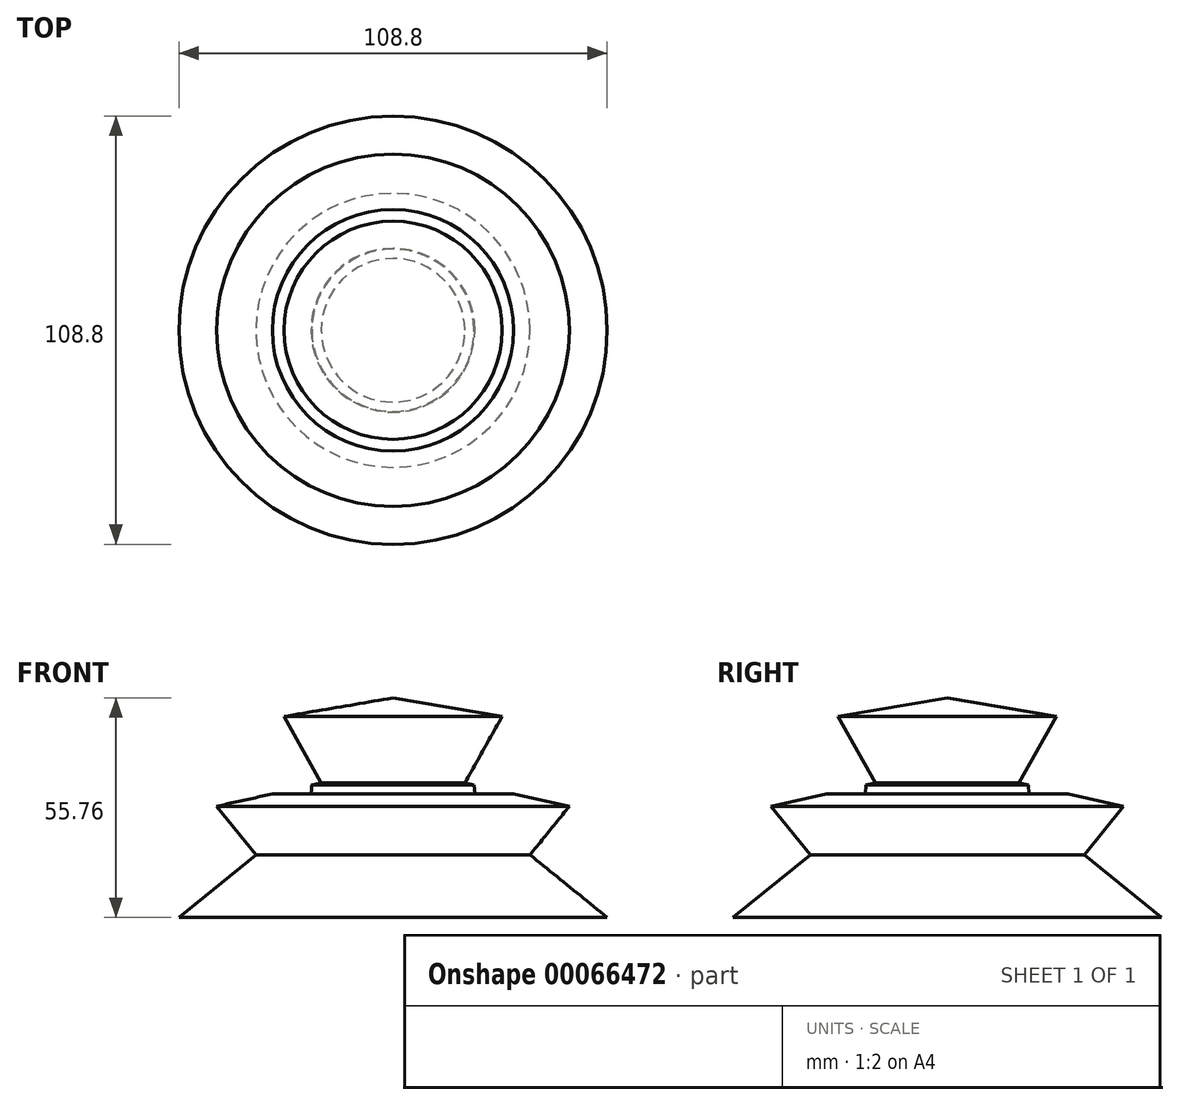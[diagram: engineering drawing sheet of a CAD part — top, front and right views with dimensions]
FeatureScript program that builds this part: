
annotation { "Feature Type Name" : "Feature", "Feature Type Description" : "" }
export const myFeature = defineFeature(function(context is Context, id is Id, definition is map)
    precondition{}
    {
        {
            var Q0;
            Q0=qCreatedBy(makeId("Front.planeOp"),FACE);
            var sketch = newSketch(context, id + "F0", { "sketchPlane" : qUnion([Q0])});
            skLineSegment(sketch, "E0", {"start": v(0, 55.76) * mm, "end": v(0, 0) * mm});
            skLineSegment(sketch, "E1", {"start": v(0, 0) * mm, "end": v(54.4, 0) * mm});
            skLineSegment(sketch, "E2", {"start": v(54.4, 0) * mm, "end": v(34.8, 15.88) * mm});
            skLineSegment(sketch, "E3", {"start": v(34.8, 15.88) * mm, "end": v(44.8, 28.21) * mm});
            skLineSegment(sketch, "E4", {"start": v(44.8, 28.21) * mm, "end": v(18.25, 34.13) * mm});
            skLineSegment(sketch, "E5", {"start": v(18.25, 34.13) * mm, "end": v(27.7, 51.02) * mm});
            skLineSegment(sketch, "E6", {"start": v(27.7, 51.02) * mm, "end": v(0, 55.76) * mm});
            skSolve(sketch);
        }
        {
            var Q0;
            Q0=makeQuery(id+"F0.imprint","IMPRINT",FACE,{"disambiguationData":[TD([[makeQuery(id+"F0.imprint","IMPRINT",EDGE,{"derivedFrom":sQuery(id+"F0.wireOp",EDGE,"E0")}),1.0]])]});
            var Q1;
            Q1=sQuery(id+"F0.wireOp",EDGE,"E0");
            revolve(context, id + "F1", {"entities" : qUnion([Q0]), "axis" : qUnion([Q1]), "revolveType" : RevolveType.FULL});
        }
        {
            var Q0;
            Q0=qCreatedBy(makeId("Right.planeOp"),FACE);
            var sketch = newSketch(context, id + "F2", { "sketchPlane" : qUnion([Q0])});
            skLineSegment(sketch, "E7", {"start": v(-20.62, 33.62) * mm, "end": v(-31, 31.36) * mm});
            skLineSegment(sketch, "E8", {"start": v(-20.8, 31.36) * mm, "end": v(-20.62, 33.62) * mm});
            skLineSegment(sketch, "E9", {"start": v(-20.8, 31.36) * mm, "end": v(-31, 31.36) * mm});
            skSolve(sketch);
        }
        {
            var Q0;
            Q0=makeQuery(id+"F2.imprint","IMPRINT",FACE,{"disambiguationData":[TD([[makeQuery(id+"F2.imprint","IMPRINT",EDGE,{"derivedFrom":sQuery(id+"F2.wireOp",EDGE,"E7")}),1.0]])]});
            var Q1;
            Q1=sQuery(id+"F2.wireOp",EDGE,"E8");
            var Q2;
            Q2=sQuery(id+"F2.wireOp",EDGE,"E9");
            var Q3;
            Q3=sQuery(id+"F2.wireOp",EDGE,"E7");
            var Q4;
            Q4=makeQuery(id+"F1.opRevolve","SWEPT_EDGE",EDGE,{"disambiguationData":[OSD([sQuery(id+"F0.wireOp",EDGE,"E3"),sQuery(id+"F0.wireOp",EDGE,"E4")])]});
            revolve(context, id + "F3", {"operationType" : NewBodyOperationType.REMOVE, "entities" : qUnion([Q0]), "surfaceEntities" : qUnion([Q1, Q2, Q3]), "axis" : qUnion([Q4]), "revolveType" : RevolveType.FULL});
        }
    });
